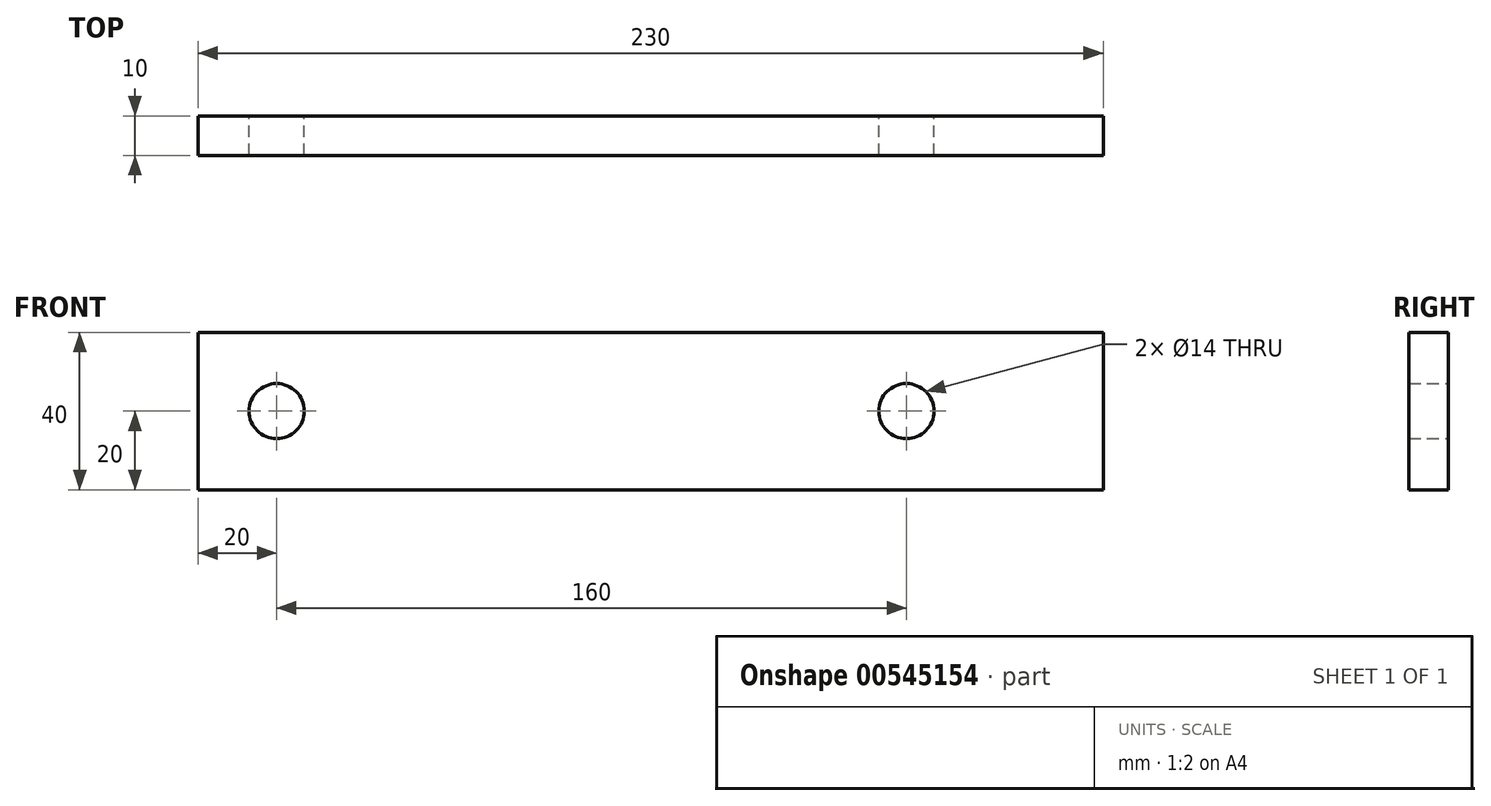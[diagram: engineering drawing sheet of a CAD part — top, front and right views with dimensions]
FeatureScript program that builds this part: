
annotation { "Feature Type Name" : "Feature", "Feature Type Description" : "" }
export const myFeature = defineFeature(function(context is Context, id is Id, definition is map)
    precondition{}
    {
        {
            var Q0;
            Q0=qCreatedBy(makeId("Front.planeOp"),FACE);
            var sketch = newSketch(context, id + "F0", { "sketchPlane" : qUnion([Q0])});
            skLineSegment(sketch, "E0.bottom", {"start": v(-115, 20) * mm, "end": v(115, 20) * mm});
            skLineSegment(sketch, "E0.top", {"start": v(-115, -20) * mm, "end": v(115, -20) * mm});
            skLineSegment(sketch, "E0.left", {"start": v(-115, 20) * mm, "end": v(-115, -20) * mm});
            skLineSegment(sketch, "E0.right", {"start": v(115, 20) * mm, "end": v(115, -20) * mm});
            skPoint(sketch, "E0.middle", {"position": v(0, 0) * mm});
            skCircle(sketch, "E1", {"center": v(-95, 0) * mm, "radius": 7 * mm});
            skCircle(sketch, "E2", {"center": v(65, 0) * mm, "radius": 7 * mm});
            skSolve(sketch);
        }
        {
            var Q0;
            Q0=makeQuery(id+"F0.imprint","IMPRINT",FACE,{"disambiguationData":[TD([[makeQuery(id+"F0.imprint","IMPRINT",EDGE,{"derivedFrom":sQuery(id+"F0.wireOp",EDGE,"E0.bottom")}),-1.0]])]});
            extrude(context, id + "F1", {"entities" : qUnion([Q0]), "depth" : 10 * mm, "offsetDistance" : 25 * mm});
        }
    });
